# Revit family: Kühlwanne Umluft EN6040 - Eigen
name_source: partatom
category: Sonderausstattung
revit_build: Autodesk Revit 2015 (Build: 20140606_1530(x64)
units: mm (PartAtom-declared; Revit-internal decimal feet)

## types (4) — shared parameters
Artikelnr. = KWMU024060
Boden Stärke = 30 mm  [stored 0.0984252 ft]
Breite Technikgehäuse = 500 mm  [stored 1.64042 ft]
DN Tauwasserabfluß = 25 mm  [stored 0.082021 ft]
Höhe = 630 mm
Höhe Technikgehäuse = 365 mm
Höhe Wanne = 265 mm  [stored 0.869423 ft]
Kapazität = 2 x EN6040, Tiefe 80 mm
Kälteleistung = 720 W / -10°C VT
Kältemittel = R404a
Material = Edelstahl AISI 304
Pole = 1
Rand Breite hinten = 44 mm
Rand Breite seitlich = 68 mm
Rand Breite vorne = 32 mm
Rand Stärke = 10 mm  [stored 0.0328084 ft]
Scheinleistung = 0 VA
Spannung = 230 V
Temp. Bereich = -1°C bis +5°C
Tiefe = 780 mm  [stored 2.55906 ft]
Tiefe ohne Rand = 738 mm
Wand Seiten Stärke = 43 mm
Wand hinten Stärke = 65 mm  [stored 0.213255 ft]
Wand vorne Stärke = 53 mm  [stored 0.173885 ft]

## per-type parameters (varying)
| type | Breite | Breite ohne Rand | Watt |
| 2xEN6040 | 950 mm  [stored 3.1168 ft] | 900 mm | 700 W |
| 3xEN6040 | 1350 mm | 1300 mm | 900 W |
| 4xEN6040 | 1750 mm | 1700 mm | 1100 W |
| 5xEN6040 | 2150 mm | 2100 mm | 1100 W |

note: [stored X ft] marks values corroborated as IEEE doubles in the binary element streams (Revit-internal decimal feet)

## geometry (parser evidence)
native form markers: Blend x14, Sweep x3
no freeform markers — native parametric forms only
